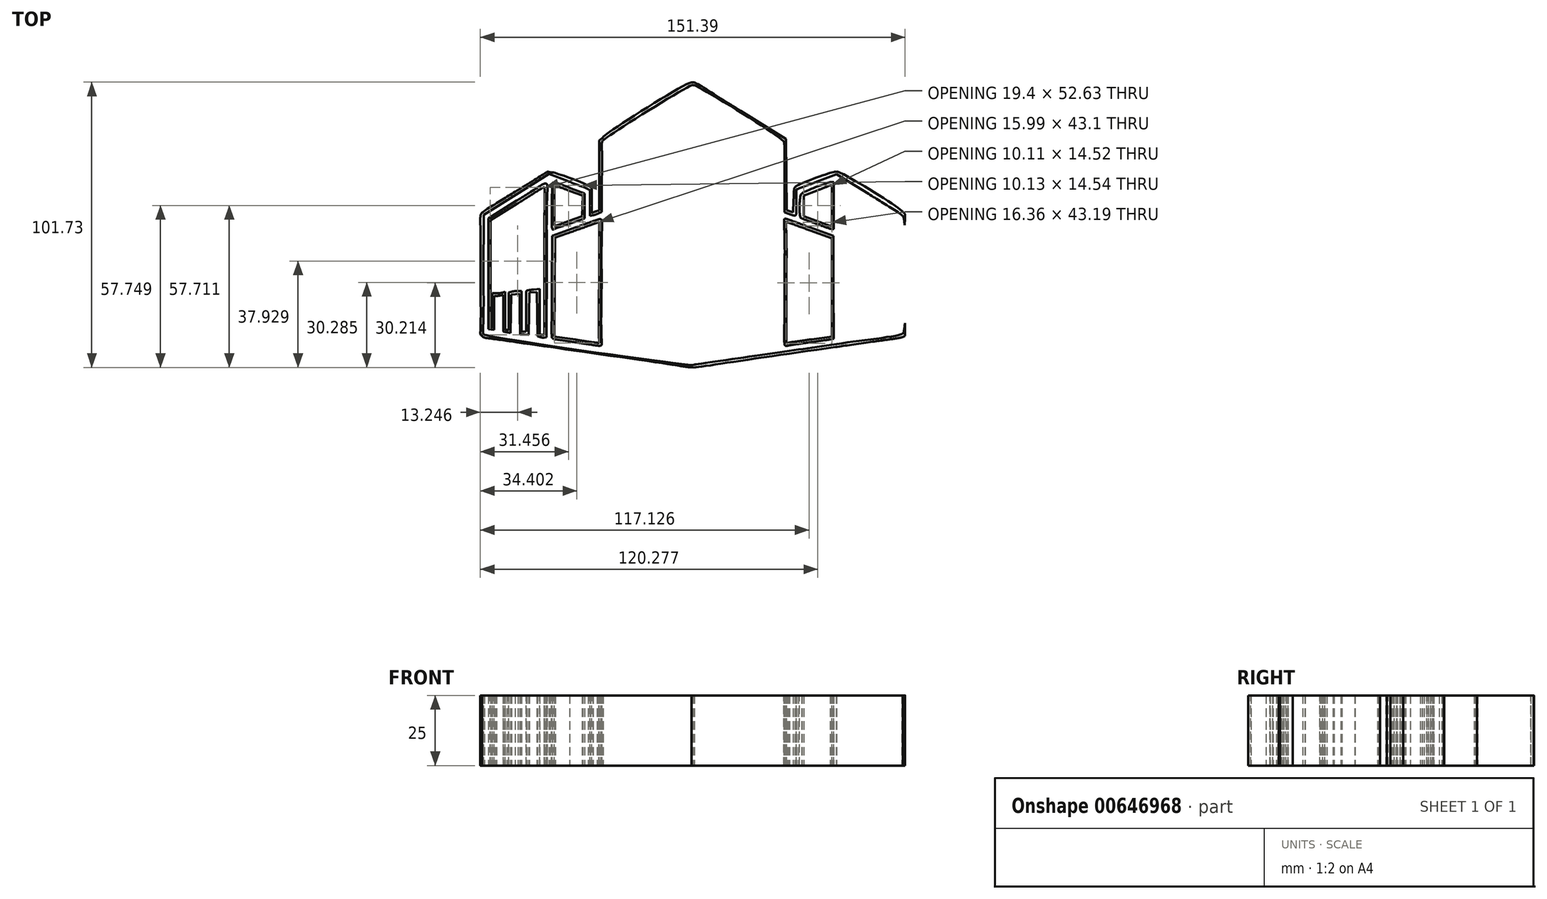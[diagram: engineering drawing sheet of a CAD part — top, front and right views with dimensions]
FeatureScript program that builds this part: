
annotation { "Feature Type Name" : "Feature", "Feature Type Description" : "" }
export const myFeature = defineFeature(function(context is Context, id is Id, definition is map)
    precondition{}
    {
        {
            var Q0;
            Q0=qCreatedBy(makeId("Top.planeOp"),FACE);
            var sketch = newSketch(context, id + "F0", { "sketchPlane" : qUnion([Q0])});
            skFitSpline(sketch, "E0", {"points": [v(-114.85, -77.61) * mm, v(-115.26, -77.27) * mm, v(-115.37, -76.9) * mm, v(-115.21, -76.34) * mm]});
            skFitSpline(sketch, "E1", {"points": [v(34.93, -23.44) * mm, v(31.93, -22.97) * mm, v(1.1, -18.5) * mm, v(-22.97, -15.06) * mm]});
            skFitSpline(sketch, "E2", {"points": [v(-22.97, -15.06) * mm, v(-31.14, -13.89) * mm, v(-35.02, -13.19) * mm, v(-35.42, -12.82) * mm]});
            skFitSpline(sketch, "E3", {"points": [v(-35.42, -12.82) * mm, v(-35.95, -12.32) * mm, v(-35.98, -10.82) * mm, v(-35.98, 9) * mm]});
            skFitSpline(sketch, "E4", {"points": [v(-35.98, 9) * mm, v(-35.98, 25.48) * mm, v(-35.9, 30.43) * mm, v(-35.58, 30.88) * mm]});
            skFitSpline(sketch, "E5", {"points": [v(-35.58, 30.88) * mm, v(-35.35, 31.2) * mm, v(-30, 34.68) * mm, v(-23.7, 38.6) * mm]});
            skFitSpline(sketch, "E6", {"points": [v(-23.7, 38.6) * mm, v(-13.38, 45.02) * mm, v(-12.09, 45.73) * mm, v(-11, 45.58) * mm]});
            skFitSpline(sketch, "E7", {"points": [v(-11, 45.58) * mm, v(-9.58, 45.39) * mm, v(2.65, 40.76) * mm, v(3.27, 40.18) * mm]});
            skFitSpline(sketch, "E8", {"points": [v(3.27, 40.18) * mm, v(3.58, 39.9) * mm, v(3.7, 38.59) * mm, v(3.7, 35.43) * mm]});
            skFitSpline(sketch, "E9", {"points": [v(3.7, 35.43) * mm, v(3.7, 31.6) * mm, v(3.76, 31.1) * mm, v(4.22, 31.3) * mm]});
            skFitSpline(sketch, "E10", {"points": [v(4.22, 31.3) * mm, v(4.5, 31.43) * mm, v(5.1, 31.62) * mm, v(5.52, 31.75) * mm]});
            skFitSpline(sketch, "E11", {"points": [v(7.36, 57.77) * mm, v(9.81, 59.8) * mm, v(38.9, 77.62) * mm, v(39.74, 77.61) * mm]});
            skFitSpline(sketch, "E12", {"points": [v(39.74, 77.61) * mm, v(40.28, 77.6) * mm, v(46.84, 73.7) * mm, v(56.73, 67.51) * mm]});
            skFitSpline(sketch, "E13", {"points": [v(75.6, 35.54) * mm, v(75.68, 37.9) * mm, v(75.9, 39.99) * mm, v(76.08, 40.17) * mm]});
            skFitSpline(sketch, "E14", {"points": [v(76.08, 40.17) * mm, v(76.62, 40.73) * mm, v(89.88, 45.68) * mm, v(90.82, 45.68) * mm]});
            skFitSpline(sketch, "E15", {"points": [v(90.82, 45.68) * mm, v(91.62, 45.68) * mm, v(113.31, 32.55) * mm, v(114.71, 31.23) * mm]});
            skFitSpline(sketch, "E16", {"points": [v(114.71, 31.23) * mm, v(115.24, 30.72) * mm, v(115.28, 29.2) * mm, v(115.28, 8.96) * mm]});
            skLineSegment(sketch, "E17", {"start": v(5.52, 31.75) * mm, "end": v(6.3, 31.96) * mm});
            skLineSegment(sketch, "E18", {"start": v(6.3, 31.96) * mm, "end": v(6.3, 44.43) * mm});
            skLineSegment(sketch, "E19", {"start": v(6.3, 44.43) * mm, "end": v(6.3, 56.9) * mm});
            skLineSegment(sketch, "E20", {"start": v(6.3, 56.9) * mm, "end": v(7.36, 57.77) * mm});
            skFitSpline(sketch, "E21", {"points": [v(114.55, -13.1) * mm, v(114.15, -13.3) * mm, v(110.82, -13.86) * mm, v(107.15, -14.37) * mm]});
            skFitSpline(sketch, "E22", {"points": [v(107.15, -14.37) * mm, v(103.48, -14.89) * mm, v(96.02, -15.95) * mm, v(90.56, -16.74) * mm]});
            skFitSpline(sketch, "E23", {"points": [v(90.56, -16.74) * mm, v(49.54, -22.69) * mm, v(40.18, -24) * mm, v(39.17, -23.97) * mm]});
            skFitSpline(sketch, "E24", {"points": [v(39.17, -23.97) * mm, v(38.54, -23.95) * mm, v(36.63, -23.71) * mm, v(34.93, -23.44) * mm]});
            skLineSegment(sketch, "E25", {"start": v(56.73, 67.51) * mm, "end": v(72.83, 57.42) * mm});
            skLineSegment(sketch, "E26", {"start": v(72.83, 57.42) * mm, "end": v(73, 44.74) * mm});
            skLineSegment(sketch, "E27", {"start": v(73, 44.74) * mm, "end": v(73.15, 32.07) * mm});
            skLineSegment(sketch, "E28", {"start": v(73.15, 32.07) * mm, "end": v(74.3, 31.66) * mm});
            skLineSegment(sketch, "E29", {"start": v(74.3, 31.66) * mm, "end": v(75.43, 31.24) * mm});
            skLineSegment(sketch, "E30", {"start": v(75.43, 31.24) * mm, "end": v(75.6, 35.54) * mm});
            skFitSpline(sketch, "E31", {"points": [v(77.34, -17.66) * mm, v(97.36, -14.77) * mm, v(113.94, -12.22) * mm, v(114.18, -12) * mm]});
            skFitSpline(sketch, "E32", {"points": [v(114.18, -12) * mm, v(114.81, -11.41) * mm, v(114.85, 29.25) * mm, v(114.22, 30.15) * mm]});
            skFitSpline(sketch, "E33", {"points": [v(114.22, 30.15) * mm, v(114, 30.47) * mm, v(108.67, 33.93) * mm, v(102.37, 37.84) * mm]});
            skFitSpline(sketch, "E34", {"points": [v(83.83, 42.23) * mm, v(79.94, 40.73) * mm, v(76.7, 39.5) * mm, v(76.66, 39.5) * mm]});
            skFitSpline(sketch, "E35", {"points": [v(76.66, 39.5) * mm, v(76.61, 39.5) * mm, v(76.57, 37.48) * mm, v(76.57, 35) * mm]});
            skFitSpline(sketch, "E36", {"points": [v(76.57, 35) * mm, v(76.57, 32.4) * mm, v(76.43, 30.38) * mm, v(76.25, 30.25) * mm]});
            skFitSpline(sketch, "E37", {"points": [v(76.25, 30.25) * mm, v(76.07, 30.13) * mm, v(75.12, 30.32) * mm, v(74.13, 30.66) * mm]});
            skLineSegment(sketch, "E38", {"start": v(115.28, 8.96) * mm, "end": v(115.28, -12.77) * mm});
            skLineSegment(sketch, "E39", {"start": v(115.28, -12.77) * mm, "end": v(114.55, -13.1) * mm});
            skFitSpline(sketch, "E40", {"points": [v(72.34, 43.66) * mm, v(72.34, 50.46) * mm, v(72.22, 56.2) * mm, v(72.1, 56.42) * mm]});
            skFitSpline(sketch, "E41", {"points": [v(72.1, 56.42) * mm, v(71.77, 56.96) * mm, v(40.43, 76.56) * mm, v(39.8, 76.62) * mm]});
            skFitSpline(sketch, "E42", {"points": [v(39.8, 76.62) * mm, v(39.36, 76.67) * mm, v(8.83, 57.85) * mm, v(7.69, 56.84) * mm]});
            skFitSpline(sketch, "E43", {"points": [v(7.69, 56.84) * mm, v(7.38, 56.56) * mm, v(7.28, 53.55) * mm, v(7.28, 43.98) * mm]});
            skLineSegment(sketch, "E44", {"start": v(102.37, 37.84) * mm, "end": v(90.92, 44.95) * mm});
            skLineSegment(sketch, "E45", {"start": v(90.92, 44.95) * mm, "end": v(83.83, 42.23) * mm});
            skFitSpline(sketch, "E46", {"points": [v(6.22, 31) * mm, v(5.64, 30.73) * mm, v(4.7, 30.4) * mm, v(4.1, 30.26) * mm]});
            skLineSegment(sketch, "E47", {"start": v(74.13, 30.66) * mm, "end": v(72.34, 31.3) * mm});
            skLineSegment(sketch, "E48", {"start": v(72.34, 31.3) * mm, "end": v(72.34, 43.66) * mm});
            skFitSpline(sketch, "E49", {"points": [v(3.05, 34.57) * mm, v(3.05, 38.73) * mm, v(3, 39.15) * mm, v(2.41, 39.5) * mm]});
            skFitSpline(sketch, "E50", {"points": [v(2.41, 39.5) * mm, v(2.06, 39.71) * mm, v(-1.23, 41.03) * mm, v(-4.89, 42.43) * mm]});
            skLineSegment(sketch, "E51", {"start": v(7.28, 43.98) * mm, "end": v(7.28, 31.49) * mm});
            skLineSegment(sketch, "E52", {"start": v(7.28, 31.49) * mm, "end": v(6.22, 31) * mm});
            skFitSpline(sketch, "E53", {"points": [v(-34.93, 9.18) * mm, v(-35, -8.5) * mm, v(-34.94, -12.08) * mm, v(-34.57, -12.24) * mm]});
            skFitSpline(sketch, "E54", {"points": [v(-34.57, -12.24) * mm, v(-33.8, -12.57) * mm, v(39.61, -23.14) * mm, v(40.3, -23.02) * mm]});
            skFitSpline(sketch, "E55", {"points": [v(40.3, -23.02) * mm, v(40.66, -22.96) * mm, v(57.33, -20.54) * mm, v(77.34, -17.66) * mm]});
            skLineSegment(sketch, "E56", {"start": v(4.1, 30.26) * mm, "end": v(3.05, 30.01) * mm});
            skLineSegment(sketch, "E57", {"start": v(3.05, 30.01) * mm, "end": v(3.05, 34.57) * mm});
            skLineSegment(sketch, "E58", {"start": v(-4.89, 42.43) * mm, "end": v(-11.54, 44.97) * mm});
            skLineSegment(sketch, "E59", {"start": v(-11.54, 44.97) * mm, "end": v(-23.2, 37.7) * mm});
            skLineSegment(sketch, "E60", {"start": v(-23.2, 37.7) * mm, "end": v(-34.85, 30.42) * mm});
            skLineSegment(sketch, "E61", {"start": v(-34.85, 30.42) * mm, "end": v(-34.93, 9.18) * mm});
            skFitSpline(sketch, "E62", {"points": [v(32.4, 7.65) * mm, v(31.56, 7.59) * mm, v(30.54, 7.46) * mm, v(30.13, 7.36) * mm]});
            skLineSegment(sketch, "E63", {"start": v(77.34, -17.66) * mm, "end": v(77.34, -17.66) * mm});
            skFitSpline(sketch, "E64", {"points": [v(24.56, 6.84) * mm, v(23.87, 6.84) * mm, v(22.85, 6.74) * mm, v(22.29, 6.62) * mm]});
            skLineSegment(sketch, "E65", {"start": v(35.1, -20.43) * mm, "end": v(34.12, -20.2) * mm});
            skLineSegment(sketch, "E66", {"start": v(34.12, -20.2) * mm, "end": v(34.03, -6.22) * mm});
            skLineSegment(sketch, "E67", {"start": v(34.03, -6.22) * mm, "end": v(33.95, 7.75) * mm});
            skLineSegment(sketch, "E68", {"start": v(33.95, 7.75) * mm, "end": v(32.4, 7.65) * mm});
            skFitSpline(sketch, "E69", {"points": [v(19.9, -18.13) * mm, v(19.24, -18.2) * mm, v(18.4, -18.07) * mm, v(18.03, -17.85) * mm]});
            skFitSpline(sketch, "E70", {"points": [v(18.03, -17.85) * mm, v(17.38, -17.46) * mm, v(17.37, -17.16) * mm, v(17.37, -5.62) * mm]});
            skLineSegment(sketch, "E71", {"start": v(30.13, 7.36) * mm, "end": v(29.4, 7.2) * mm});
            skLineSegment(sketch, "E72", {"start": v(29.4, 7.2) * mm, "end": v(29.4, -6.07) * mm});
            skLineSegment(sketch, "E73", {"start": v(29.4, -6.07) * mm, "end": v(29.4, -19.33) * mm});
            skLineSegment(sketch, "E74", {"start": v(29.4, -19.33) * mm, "end": v(27.7, -19.22) * mm});
            skLineSegment(sketch, "E75", {"start": v(27.7, -19.22) * mm, "end": v(25.99, -19.11) * mm});
            skLineSegment(sketch, "E76", {"start": v(25.99, -19.11) * mm, "end": v(25.9, -6.13) * mm});
            skLineSegment(sketch, "E77", {"start": v(25.9, -6.13) * mm, "end": v(25.81, 6.84) * mm});
            skLineSegment(sketch, "E78", {"start": v(25.81, 6.84) * mm, "end": v(24.56, 6.84) * mm});
            skFitSpline(sketch, "E79", {"points": [v(15.66, 5.99) * mm, v(14.72, 5.86) * mm, v(13.7, 5.76) * mm, v(13.38, 5.76) * mm]});
            skFitSpline(sketch, "E80", {"points": [v(13.38, 5.76) * mm, v(12.85, 5.75) * mm, v(12.81, 4.96) * mm, v(12.81, -5.73) * mm]});
            skLineSegment(sketch, "E81", {"start": v(22.29, 6.62) * mm, "end": v(21.28, 6.39) * mm});
            skLineSegment(sketch, "E82", {"start": v(21.28, 6.39) * mm, "end": v(21.2, -5.82) * mm});
            skLineSegment(sketch, "E83", {"start": v(21.2, -5.82) * mm, "end": v(21.1, -18.02) * mm});
            skLineSegment(sketch, "E84", {"start": v(21.1, -18.02) * mm, "end": v(19.9, -18.13) * mm});
            skFitSpline(sketch, "E85", {"points": [v(11.1, -16.96) * mm, v(10.16, -16.82) * mm, v(9.28, -16.58) * mm, v(9.15, -16.44) * mm]});
            skFitSpline(sketch, "E86", {"points": [v(9.15, -16.44) * mm, v(9.01, -16.29) * mm, v(8.94, -0.04) * mm, v(8.99, 19.67) * mm]});
            skLineSegment(sketch, "E87", {"start": v(17.37, -5.62) * mm, "end": v(17.37, 6.22) * mm});
            skLineSegment(sketch, "E88", {"start": v(17.37, 6.22) * mm, "end": v(15.66, 5.99) * mm});
            skFitSpline(sketch, "E89", {"points": [v(10.49, 56.4) * mm, v(11.26, 56.89) * mm, v(12.03, 57.3) * mm, v(12.2, 57.3) * mm]});
            skFitSpline(sketch, "E90", {"points": [v(12.2, 57.3) * mm, v(12.36, 57.3) * mm, v(12.49, 52) * mm, v(12.49, 44.93) * mm]});
            skLineSegment(sketch, "E91", {"start": v(12.81, -5.73) * mm, "end": v(12.81, -17.2) * mm});
            skLineSegment(sketch, "E92", {"start": v(12.81, -17.2) * mm, "end": v(11.1, -16.96) * mm});
            skFitSpline(sketch, "E93", {"points": [v(13.22, 32.82) * mm, v(13.62, 32.96) * mm, v(14.68, 33.36) * mm, v(15.58, 33.7) * mm]});
            skLineSegment(sketch, "E94", {"start": v(8.99, 19.67) * mm, "end": v(9.07, 55.5) * mm});
            skLineSegment(sketch, "E95", {"start": v(9.07, 55.5) * mm, "end": v(10.49, 56.4) * mm});
            skFitSpline(sketch, "E96", {"points": [v(18.75, 61.56) * mm, v(19.5, 62) * mm, v(20.31, 62.38) * mm, v(20.54, 62.38) * mm]});
            skFitSpline(sketch, "E97", {"points": [v(20.54, 62.38) * mm, v(20.85, 62.37) * mm, v(20.94, 59.45) * mm, v(20.94, 49) * mm]});
            skLineSegment(sketch, "E98", {"start": v(12.49, 44.93) * mm, "end": v(12.49, 32.56) * mm});
            skLineSegment(sketch, "E99", {"start": v(12.49, 32.56) * mm, "end": v(13.22, 32.82) * mm});
            skFitSpline(sketch, "E100", {"points": [v(26.8, 66.54) * mm, v(29.22, 68.26) * mm, v(29.08, 69.14) * mm, v(29.08, 52.99) * mm]});
            skLineSegment(sketch, "E101", {"start": v(15.58, 33.7) * mm, "end": v(17.2, 34.31) * mm});
            skLineSegment(sketch, "E102", {"start": v(17.2, 34.31) * mm, "end": v(17.29, 47.53) * mm});
            skLineSegment(sketch, "E103", {"start": v(17.29, 47.53) * mm, "end": v(17.37, 60.75) * mm});
            skLineSegment(sketch, "E104", {"start": v(17.37, 60.75) * mm, "end": v(18.75, 61.56) * mm});
            skFitSpline(sketch, "E105", {"points": [v(35.9, 72.26) * mm, v(37.07, 73) * mm, v(38.2, 73.63) * mm, v(38.43, 73.63) * mm]});
            skFitSpline(sketch, "E106", {"points": [v(38.43, 73.63) * mm, v(38.75, 73.63) * mm, v(38.84, 64.04) * mm, v(38.84, 26.44) * mm]});
            skLineSegment(sketch, "E107", {"start": v(20.94, 49) * mm, "end": v(20.94, 35.6) * mm});
            skLineSegment(sketch, "E108", {"start": v(20.94, 35.6) * mm, "end": v(23.22, 36.38) * mm});
            skLineSegment(sketch, "E109", {"start": v(23.22, 36.38) * mm, "end": v(25.5, 37.15) * mm});
            skLineSegment(sketch, "E110", {"start": v(25.5, 37.15) * mm, "end": v(25.5, 51.4) * mm});
            skLineSegment(sketch, "E111", {"start": v(25.5, 51.4) * mm, "end": v(25.5, 65.63) * mm});
            skLineSegment(sketch, "E112", {"start": v(25.5, 65.63) * mm, "end": v(26.8, 66.54) * mm});
            skFitSpline(sketch, "E113", {"points": [v(37.45, -20.7) * mm, v(36.7, -20.68) * mm, v(35.63, -20.55) * mm, v(35.1, -20.42) * mm]});
            skLineSegment(sketch, "E114", {"start": v(29.08, 52.99) * mm, "end": v(29.08, 38.52) * mm});
            skLineSegment(sketch, "E115", {"start": v(29.08, 38.52) * mm, "end": v(31.35, 39.27) * mm});
            skLineSegment(sketch, "E116", {"start": v(31.35, 39.27) * mm, "end": v(33.62, 40.01) * mm});
            skLineSegment(sketch, "E117", {"start": v(33.62, 40.01) * mm, "end": v(33.7, 55.45) * mm});
            skLineSegment(sketch, "E118", {"start": v(33.7, 55.45) * mm, "end": v(33.8, 70.88) * mm});
            skLineSegment(sketch, "E119", {"start": v(33.8, 70.88) * mm, "end": v(35.9, 72.26) * mm});
            skFitSpline(sketch, "E120", {"points": [v(31.84, 38.36) * mm, v(30.4, 37.83) * mm, v(29.06, 37.38) * mm, v(28.83, 37.36) * mm]});
            skFitSpline(sketch, "E121", {"points": [v(28.83, 37.36) * mm, v(28.51, 37.34) * mm, v(28.43, 40.46) * mm, v(28.43, 51.86) * mm]});
            skLineSegment(sketch, "E122", {"start": v(38.84, 26.44) * mm, "end": v(38.84, -20.74) * mm});
            skLineSegment(sketch, "E123", {"start": v(38.84, -20.74) * mm, "end": v(37.45, -20.7) * mm});
            skFitSpline(sketch, "E124", {"points": [v(23.55, 35.43) * mm, v(22.03, 34.88) * mm, v(20.6, 34.5) * mm, v(20.37, 34.6) * mm]});
            skFitSpline(sketch, "E125", {"points": [v(20.37, 34.6) * mm, v(20.06, 34.73) * mm, v(19.97, 37.71) * mm, v(19.97, 47.84) * mm]});
            skFitSpline(sketch, "E126", {"points": [v(19.97, 47.84) * mm, v(19.97, 55.04) * mm, v(19.85, 60.92) * mm, v(19.71, 60.92) * mm]});
            skFitSpline(sketch, "E127", {"points": [v(19.71, 60.92) * mm, v(19.58, 60.92) * mm, v(19.14, 60.67) * mm, v(18.74, 60.36) * mm]});
            skLineSegment(sketch, "E128", {"start": v(37.86, 26.27) * mm, "end": v(37.86, 72.19) * mm});
            skLineSegment(sketch, "E129", {"start": v(37.86, 72.19) * mm, "end": v(36.24, 71.27) * mm});
            skLineSegment(sketch, "E130", {"start": v(36.24, 71.27) * mm, "end": v(34.61, 70.35) * mm});
            skLineSegment(sketch, "E131", {"start": v(34.61, 70.35) * mm, "end": v(34.53, 54.84) * mm});
            skLineSegment(sketch, "E132", {"start": v(34.53, 54.84) * mm, "end": v(34.44, 39.33) * mm});
            skLineSegment(sketch, "E133", {"start": v(34.44, 39.33) * mm, "end": v(31.84, 38.36) * mm});
            skFitSpline(sketch, "E134", {"points": [v(15.31, 32.5) * mm, v(13.83, 31.96) * mm, v(12.44, 31.52) * mm, v(12.22, 31.52) * mm]});
            skFitSpline(sketch, "E135", {"points": [v(12.22, 31.52) * mm, v(11.93, 31.52) * mm, v(11.84, 34.52) * mm, v(11.84, 43.68) * mm]});
            skFitSpline(sketch, "E136", {"points": [v(11.84, 43.68) * mm, v(11.84, 50.54) * mm, v(11.7, 55.84) * mm, v(11.55, 55.84) * mm]});
            skFitSpline(sketch, "E137", {"points": [v(11.55, 55.84) * mm, v(11.39, 55.84) * mm, v(10.94, 55.56) * mm, v(10.56, 55.2) * mm]});
            skLineSegment(sketch, "E138", {"start": v(28.43, 51.86) * mm, "end": v(28.43, 66.39) * mm});
            skLineSegment(sketch, "E139", {"start": v(28.43, 66.39) * mm, "end": v(27.45, 65.82) * mm});
            skLineSegment(sketch, "E140", {"start": v(27.45, 65.82) * mm, "end": v(26.48, 65.26) * mm});
            skLineSegment(sketch, "E141", {"start": v(26.48, 65.26) * mm, "end": v(26.4, 50.85) * mm});
            skLineSegment(sketch, "E142", {"start": v(26.4, 50.85) * mm, "end": v(26.31, 36.43) * mm});
            skLineSegment(sketch, "E143", {"start": v(26.31, 36.43) * mm, "end": v(23.55, 35.43) * mm});
            skFitSpline(sketch, "E144", {"points": [v(12.9, 6.63) * mm, v(13.3, 6.72) * mm, v(14.69, 6.9) * mm, v(15.98, 7.02) * mm]});
            skLineSegment(sketch, "E145", {"start": v(18.74, 60.36) * mm, "end": v(18.02, 59.8) * mm});
            skLineSegment(sketch, "E146", {"start": v(18.02, 59.8) * mm, "end": v(18.02, 46.64) * mm});
            skLineSegment(sketch, "E147", {"start": v(18.02, 46.64) * mm, "end": v(18.02, 33.49) * mm});
            skLineSegment(sketch, "E148", {"start": v(18.02, 33.49) * mm, "end": v(15.31, 32.5) * mm});
            skFitSpline(sketch, "E149", {"points": [v(20.3, -4.98) * mm, v(20.3, 1.7) * mm, v(20.4, 7.23) * mm, v(20.54, 7.32) * mm]});
            skFitSpline(sketch, "E150", {"points": [v(20.54, 7.32) * mm, v(20.67, 7.4) * mm, v(22.06, 7.6) * mm, v(23.63, 7.74) * mm]});
            skLineSegment(sketch, "E151", {"start": v(10.56, 55.2) * mm, "end": v(9.87, 54.57) * mm});
            skLineSegment(sketch, "E152", {"start": v(9.87, 54.57) * mm, "end": v(9.96, 19.36) * mm});
            skLineSegment(sketch, "E153", {"start": v(9.96, 19.36) * mm, "end": v(10.05, -15.84) * mm});
            skLineSegment(sketch, "E154", {"start": v(10.05, -15.84) * mm, "end": v(11.1, -15.96) * mm});
            skLineSegment(sketch, "E155", {"start": v(11.1, -15.96) * mm, "end": v(12.16, -16.07) * mm});
            skLineSegment(sketch, "E156", {"start": v(12.16, -16.07) * mm, "end": v(12.16, -4.8) * mm});
            skLineSegment(sketch, "E157", {"start": v(12.16, -4.8) * mm, "end": v(12.16, 6.46) * mm});
            skLineSegment(sketch, "E158", {"start": v(12.16, 6.46) * mm, "end": v(12.9, 6.63) * mm});
            skFitSpline(sketch, "E159", {"points": [v(26.47, -5.1) * mm, v(26.47, -16.17) * mm, v(26.55, -18.2) * mm, v(26.94, -18.2) * mm]});
            skFitSpline(sketch, "E160", {"points": [v(26.94, -18.2) * mm, v(27.19, -18.2) * mm, v(27.63, -18.3) * mm, v(27.9, -18.42) * mm]});
            skFitSpline(sketch, "E161", {"points": [v(27.9, -18.42) * mm, v(28.36, -18.62) * mm, v(28.43, -17.24) * mm, v(28.5, -5.26) * mm]});
            skLineSegment(sketch, "E162", {"start": v(15.98, 7.02) * mm, "end": v(18.34, 7.25) * mm});
            skLineSegment(sketch, "E163", {"start": v(18.34, 7.25) * mm, "end": v(18.34, -4.93) * mm});
            skLineSegment(sketch, "E164", {"start": v(18.34, -4.93) * mm, "end": v(18.34, -17.11) * mm});
            skLineSegment(sketch, "E165", {"start": v(18.34, -17.11) * mm, "end": v(19.32, -17.11) * mm});
            skLineSegment(sketch, "E166", {"start": v(19.32, -17.11) * mm, "end": v(20.3, -17.11) * mm});
            skLineSegment(sketch, "E167", {"start": v(20.3, -17.11) * mm, "end": v(20.3, -4.98) * mm});
            skFitSpline(sketch, "E168", {"points": [v(31.25, 8.43) * mm, v(32.72, 8.6) * mm, v(34.14, 8.65) * mm, v(34.42, 8.53) * mm]});
            skFitSpline(sketch, "E169", {"points": [v(34.42, 8.53) * mm, v(34.87, 8.34) * mm, v(34.93, 6.7) * mm, v(34.93, -5.43) * mm]});
            skFitSpline(sketch, "E170", {"points": [v(34.93, -5.43) * mm, v(34.93, -12.99) * mm, v(35.03, -19.28) * mm, v(35.15, -19.41) * mm]});
            skFitSpline(sketch, "E171", {"points": [v(35.15, -19.41) * mm, v(35.27, -19.55) * mm, v(35.93, -19.65) * mm, v(36.61, -19.65) * mm]});
            skLineSegment(sketch, "E172", {"start": v(23.63, 7.74) * mm, "end": v(26.47, 8) * mm});
            skLineSegment(sketch, "E173", {"start": v(26.47, 8) * mm, "end": v(26.47, -5.1) * mm});
            skFitSpline(sketch, "E174", {"points": [v(40.79, 26.4) * mm, v(40.79, 52.86) * mm, v(40.91, 73.63) * mm, v(41.07, 73.63) * mm]});
            skFitSpline(sketch, "E175", {"points": [v(41.07, 73.63) * mm, v(41.22, 73.63) * mm, v(42.32, 73.03) * mm, v(43.5, 72.3) * mm]});
            skLineSegment(sketch, "E176", {"start": v(28.5, -5.26) * mm, "end": v(28.59, 8.11) * mm});
            skLineSegment(sketch, "E177", {"start": v(28.59, 8.11) * mm, "end": v(31.25, 8.43) * mm});
            skFitSpline(sketch, "E178", {"points": [v(50.22, 52.96) * mm, v(50.22, 69.14) * mm, v(50.06, 68.2) * mm, v(52.5, 66.64) * mm]});
            skLineSegment(sketch, "E179", {"start": v(36.61, -19.65) * mm, "end": v(37.86, -19.65) * mm});
            skLineSegment(sketch, "E180", {"start": v(37.86, -19.65) * mm, "end": v(37.86, 26.27) * mm});
            skFitSpline(sketch, "E181", {"points": [v(55.59, 36.6) * mm, v(56.48, 36.26) * mm, v(57.54, 35.87) * mm, v(57.95, 35.73) * mm]});
            skLineSegment(sketch, "E182", {"start": v(43.5, 72.3) * mm, "end": v(45.66, 70.95) * mm});
            skLineSegment(sketch, "E183", {"start": v(45.66, 70.95) * mm, "end": v(45.74, 55.54) * mm});
            skLineSegment(sketch, "E184", {"start": v(45.74, 55.54) * mm, "end": v(45.83, 40.12) * mm});
            skLineSegment(sketch, "E185", {"start": v(45.83, 40.12) * mm, "end": v(48.03, 39.3) * mm});
            skLineSegment(sketch, "E186", {"start": v(48.03, 39.3) * mm, "end": v(50.22, 38.47) * mm});
            skLineSegment(sketch, "E187", {"start": v(50.22, 38.47) * mm, "end": v(50.22, 52.96) * mm});
            skFitSpline(sketch, "E188", {"points": [v(58.68, 48.92) * mm, v(58.68, 58.25) * mm, v(58.79, 62.37) * mm, v(59.03, 62.37) * mm]});
            skFitSpline(sketch, "E189", {"points": [v(59.03, 62.37) * mm, v(59.22, 62.37) * mm, v(60.02, 61.95) * mm, v(60.82, 61.43) * mm]});
            skLineSegment(sketch, "E190", {"start": v(52.5, 66.64) * mm, "end": v(53.79, 65.82) * mm});
            skLineSegment(sketch, "E191", {"start": v(53.79, 65.82) * mm, "end": v(53.88, 51.52) * mm});
            skLineSegment(sketch, "E192", {"start": v(53.88, 51.52) * mm, "end": v(53.96, 37.22) * mm});
            skLineSegment(sketch, "E193", {"start": v(53.96, 37.22) * mm, "end": v(55.59, 36.6) * mm});
            skFitSpline(sketch, "E194", {"points": [v(64.13, 33.54) * mm, v(65.16, 33.18) * mm, v(66.18, 32.8) * mm, v(66.4, 32.7) * mm]});
            skFitSpline(sketch, "E195", {"points": [v(66.4, 32.7) * mm, v(66.73, 32.57) * mm, v(66.81, 35.16) * mm, v(66.81, 44.91) * mm]});
            skFitSpline(sketch, "E196", {"points": [v(66.81, 44.91) * mm, v(66.81, 53.48) * mm, v(66.92, 57.3) * mm, v(67.16, 57.3) * mm]});
            skFitSpline(sketch, "E197", {"points": [v(67.16, 57.3) * mm, v(67.35, 57.3) * mm, v(68.16, 56.87) * mm, v(68.95, 56.35) * mm]});
            skLineSegment(sketch, "E198", {"start": v(57.95, 35.73) * mm, "end": v(58.68, 35.47) * mm});
            skLineSegment(sketch, "E199", {"start": v(58.68, 35.47) * mm, "end": v(58.68, 48.92) * mm});
            skFitSpline(sketch, "E200", {"points": [v(70.39, 19.53) * mm, v(70.39, -0.2) * mm, v(70.28, -16.42) * mm, v(70.15, -16.51) * mm]});
            skFitSpline(sketch, "E201", {"points": [v(70.15, -16.51) * mm, v(70.01, -16.6) * mm, v(69.2, -16.8) * mm, v(68.36, -16.94) * mm]});
            skLineSegment(sketch, "E202", {"start": v(60.82, 61.43) * mm, "end": v(62.26, 60.5) * mm});
            skLineSegment(sketch, "E203", {"start": v(62.26, 60.5) * mm, "end": v(62.26, 47.34) * mm});
            skLineSegment(sketch, "E204", {"start": v(62.26, 47.34) * mm, "end": v(62.26, 34.2) * mm});
            skLineSegment(sketch, "E205", {"start": v(62.26, 34.2) * mm, "end": v(64.13, 33.54) * mm});
            skFitSpline(sketch, "E206", {"points": [v(65.1, 5.88) * mm, v(64.16, 6) * mm, v(63.14, 6.11) * mm, v(62.83, 6.11) * mm]});
            skFitSpline(sketch, "E207", {"points": [v(62.83, 6.11) * mm, v(62.3, 6.11) * mm, v(62.26, 5.3) * mm, v(62.26, -5.82) * mm]});
            skLineSegment(sketch, "E208", {"start": v(68.95, 56.35) * mm, "end": v(70.39, 55.4) * mm});
            skLineSegment(sketch, "E209", {"start": v(70.39, 55.4) * mm, "end": v(70.39, 19.53) * mm});
            skFitSpline(sketch, "E210", {"points": [v(61.24, -17.98) * mm, v(60.68, -18.1) * mm, v(59.88, -18.2) * mm, v(59.45, -18.2) * mm]});
            skLineSegment(sketch, "E211", {"start": v(68.36, -16.94) * mm, "end": v(66.81, -17.2) * mm});
            skLineSegment(sketch, "E212", {"start": v(66.81, -17.2) * mm, "end": v(66.81, -5.77) * mm});
            skLineSegment(sketch, "E213", {"start": v(66.81, -5.77) * mm, "end": v(66.81, 5.65) * mm});
            skLineSegment(sketch, "E214", {"start": v(66.81, 5.65) * mm, "end": v(65.1, 5.88) * mm});
            skFitSpline(sketch, "E215", {"points": [v(57.46, 6.6) * mm, v(56.79, 6.73) * mm, v(55.7, 6.84) * mm, v(55.02, 6.84) * mm]});
            skLineSegment(sketch, "E216", {"start": v(62.26, -5.82) * mm, "end": v(62.26, -17.75) * mm});
            skLineSegment(sketch, "E217", {"start": v(62.26, -17.75) * mm, "end": v(61.24, -17.98) * mm});
            skFitSpline(sketch, "E218", {"points": [v(49.49, 7.36) * mm, v(49.09, 7.46) * mm, v(48.06, 7.59) * mm, v(47.21, 7.65) * mm]});
            skLineSegment(sketch, "E219", {"start": v(59.45, -18.2) * mm, "end": v(58.68, -18.2) * mm});
            skLineSegment(sketch, "E220", {"start": v(58.68, -18.2) * mm, "end": v(58.68, -5.9) * mm});
            skLineSegment(sketch, "E221", {"start": v(58.68, -5.9) * mm, "end": v(58.68, 6.38) * mm});
            skLineSegment(sketch, "E222", {"start": v(58.68, 6.38) * mm, "end": v(57.46, 6.6) * mm});
            skFitSpline(sketch, "E223", {"points": [v(45.67, -6.11) * mm, v(45.67, -13.74) * mm, v(45.54, -20.06) * mm, v(45.4, -20.16) * mm]});
            skFitSpline(sketch, "E224", {"points": [v(45.4, -20.16) * mm, v(45.25, -20.26) * mm, v(44.15, -20.46) * mm, v(42.96, -20.6) * mm]});
            skLineSegment(sketch, "E225", {"start": v(55.02, 6.84) * mm, "end": v(53.8, 6.84) * mm});
            skLineSegment(sketch, "E226", {"start": v(53.8, 6.84) * mm, "end": v(53.72, -6.13) * mm});
            skLineSegment(sketch, "E227", {"start": v(53.72, -6.13) * mm, "end": v(53.64, -19.11) * mm});
            skLineSegment(sketch, "E228", {"start": v(53.64, -19.11) * mm, "end": v(51.93, -19.22) * mm});
            skLineSegment(sketch, "E229", {"start": v(51.93, -19.22) * mm, "end": v(50.22, -19.33) * mm});
            skLineSegment(sketch, "E230", {"start": v(50.22, -19.33) * mm, "end": v(50.22, -6.07) * mm});
            skLineSegment(sketch, "E231", {"start": v(50.22, -6.07) * mm, "end": v(50.22, 7.2) * mm});
            skLineSegment(sketch, "E232", {"start": v(50.22, 7.2) * mm, "end": v(49.49, 7.36) * mm});
            skLineSegment(sketch, "E233", {"start": v(47.21, 7.65) * mm, "end": v(45.67, 7.75) * mm});
            skLineSegment(sketch, "E234", {"start": v(45.67, 7.75) * mm, "end": v(45.67, -6.11) * mm});
            skFitSpline(sketch, "E235", {"points": [v(44.7, -5.48) * mm, v(44.7, 6.7) * mm, v(44.75, 8.34) * mm, v(45.2, 8.53) * mm]});
            skFitSpline(sketch, "E236", {"points": [v(45.2, 8.53) * mm, v(45.48, 8.65) * mm, v(46.9, 8.6) * mm, v(48.37, 8.43) * mm]});
            skLineSegment(sketch, "E237", {"start": v(42.96, -20.6) * mm, "end": v(40.79, -20.84) * mm});
            skLineSegment(sketch, "E238", {"start": v(40.79, -20.84) * mm, "end": v(40.79, 26.4) * mm});
            skFitSpline(sketch, "E239", {"points": [v(55.15, 7.8) * mm, v(56.25, 7.67) * mm, v(57.64, 7.57) * mm, v(58.24, 7.57) * mm]});
            skLineSegment(sketch, "E240", {"start": v(43.96, -19.44) * mm, "end": v(44.7, -19.28) * mm});
            skLineSegment(sketch, "E241", {"start": v(44.7, -19.28) * mm, "end": v(44.7, -5.48) * mm});
            skFitSpline(sketch, "E242", {"points": [v(63.88, 6.9) * mm, v(67.87, 6.72) * mm, v(67.46, 8.06) * mm, v(67.46, -4.82) * mm]});
            skLineSegment(sketch, "E243", {"start": v(48.37, 8.43) * mm, "end": v(51.03, 8.11) * mm});
            skLineSegment(sketch, "E244", {"start": v(51.03, 8.11) * mm, "end": v(51.12, -5.16) * mm});
            skLineSegment(sketch, "E245", {"start": v(51.12, -5.16) * mm, "end": v(51.2, -18.44) * mm});
            skLineSegment(sketch, "E246", {"start": v(51.2, -18.44) * mm, "end": v(52.18, -18.28) * mm});
            skLineSegment(sketch, "E247", {"start": v(52.18, -18.28) * mm, "end": v(53.15, -18.12) * mm});
            skLineSegment(sketch, "E248", {"start": v(53.15, -18.12) * mm, "end": v(53.15, -5.04) * mm});
            skLineSegment(sketch, "E249", {"start": v(53.15, -5.04) * mm, "end": v(53.15, 8.03) * mm});
            skLineSegment(sketch, "E250", {"start": v(53.15, 8.03) * mm, "end": v(55.15, 7.8) * mm});
            skFitSpline(sketch, "E251", {"points": [v(68.59, 55.42) * mm, v(68.13, 55.65) * mm, v(67.7, 55.84) * mm, v(67.6, 55.84) * mm]});
            skFitSpline(sketch, "E252", {"points": [v(67.6, 55.84) * mm, v(67.53, 55.84) * mm, v(67.46, 50.36) * mm, v(67.46, 43.65) * mm]});
            skLineSegment(sketch, "E253", {"start": v(58.24, 7.57) * mm, "end": v(59.33, 7.57) * mm});
            skLineSegment(sketch, "E254", {"start": v(59.33, 7.57) * mm, "end": v(59.33, -4.77) * mm});
            skLineSegment(sketch, "E255", {"start": v(59.33, -4.77) * mm, "end": v(59.33, -17.11) * mm});
            skLineSegment(sketch, "E256", {"start": v(59.33, -17.11) * mm, "end": v(60.3, -17.11) * mm});
            skLineSegment(sketch, "E257", {"start": v(60.3, -17.11) * mm, "end": v(61.27, -17.11) * mm});
            skLineSegment(sketch, "E258", {"start": v(61.27, -17.11) * mm, "end": v(61.36, -5.05) * mm});
            skLineSegment(sketch, "E259", {"start": v(61.36, -5.05) * mm, "end": v(61.44, 7.02) * mm});
            skLineSegment(sketch, "E260", {"start": v(61.44, 7.02) * mm, "end": v(63.88, 6.9) * mm});
            skFitSpline(sketch, "E261", {"points": [v(66.4, 31.72) * mm, v(65.82, 31.86) * mm, v(64.47, 32.33) * mm, v(63.4, 32.75) * mm]});
            skLineSegment(sketch, "E262", {"start": v(67.46, -4.82) * mm, "end": v(67.46, -16.07) * mm});
            skLineSegment(sketch, "E263", {"start": v(67.46, -16.07) * mm, "end": v(68.36, -15.96) * mm});
            skLineSegment(sketch, "E264", {"start": v(68.36, -15.96) * mm, "end": v(69.25, -15.84) * mm});
            skLineSegment(sketch, "E265", {"start": v(69.25, -15.84) * mm, "end": v(69.33, 19.58) * mm});
            skLineSegment(sketch, "E266", {"start": v(69.33, 19.58) * mm, "end": v(69.42, 55) * mm});
            skLineSegment(sketch, "E267", {"start": v(69.42, 55) * mm, "end": v(68.59, 55.42) * mm});
            skFitSpline(sketch, "E268", {"points": [v(60.45, 60.5) * mm, v(60, 60.73) * mm, v(59.56, 60.92) * mm, v(59.48, 60.92) * mm]});
            skFitSpline(sketch, "E269", {"points": [v(59.48, 60.92) * mm, v(59.4, 60.92) * mm, v(59.33, 54.96) * mm, v(59.33, 47.67) * mm]});
            skFitSpline(sketch, "E270", {"points": [v(59.33, 47.67) * mm, v(59.33, 40.39) * mm, v(59.22, 34.42) * mm, v(59.09, 34.42) * mm]});
            skFitSpline(sketch, "E271", {"points": [v(59.09, 34.42) * mm, v(58.95, 34.42) * mm, v(57.56, 34.85) * mm, v(56, 35.39) * mm]});
            skLineSegment(sketch, "E272", {"start": v(67.46, 43.65) * mm, "end": v(67.46, 31.47) * mm});
            skLineSegment(sketch, "E273", {"start": v(67.46, 31.47) * mm, "end": v(66.4, 31.72) * mm});
            skFitSpline(sketch, "E274", {"points": [v(52.32, 65.58) * mm, v(51.86, 65.81) * mm, v(51.43, 66) * mm, v(51.34, 66) * mm]});
            skFitSpline(sketch, "E275", {"points": [v(51.34, 66) * mm, v(51.26, 66) * mm, v(51.2, 59.64) * mm, v(51.2, 51.87) * mm]});
            skFitSpline(sketch, "E276", {"points": [v(51.2, 51.87) * mm, v(51.2, 43.57) * mm, v(51.07, 37.65) * mm, v(50.9, 37.53) * mm]});
            skFitSpline(sketch, "E277", {"points": [v(50.9, 37.53) * mm, v(50.73, 37.41) * mm, v(49.3, 37.78) * mm, v(47.72, 38.34) * mm]});
            skLineSegment(sketch, "E278", {"start": v(63.4, 32.75) * mm, "end": v(61.44, 33.52) * mm});
            skLineSegment(sketch, "E279", {"start": v(61.44, 33.52) * mm, "end": v(61.36, 46.8) * mm});
            skLineSegment(sketch, "E280", {"start": v(61.36, 46.8) * mm, "end": v(61.27, 60.08) * mm});
            skLineSegment(sketch, "E281", {"start": v(61.27, 60.08) * mm, "end": v(60.45, 60.5) * mm});
            skFitSpline(sketch, "E282", {"points": [v(43.11, 71.28) * mm, v(42.33, 71.77) * mm, v(41.64, 72.17) * mm, v(41.57, 72.17) * mm]});
            skFitSpline(sketch, "E283", {"points": [v(41.57, 72.17) * mm, v(41.5, 72.17) * mm, v(41.44, 51.45) * mm, v(41.44, 26.13) * mm]});
            skLineSegment(sketch, "E284", {"start": v(56, 35.39) * mm, "end": v(53.15, 36.36) * mm});
            skLineSegment(sketch, "E285", {"start": v(53.15, 36.36) * mm, "end": v(53.15, 50.76) * mm});
            skLineSegment(sketch, "E286", {"start": v(53.15, 50.76) * mm, "end": v(53.15, 65.16) * mm});
            skLineSegment(sketch, "E287", {"start": v(53.15, 65.16) * mm, "end": v(52.32, 65.58) * mm});
            skFitSpline(sketch, "E288", {"points": [v(42.33, -19.76) * mm, v(42.82, -19.68) * mm, v(43.56, -19.54) * mm, v(43.96, -19.44) * mm]});
            skLineSegment(sketch, "E289", {"start": v(47.72, 38.34) * mm, "end": v(44.85, 39.36) * mm});
            skLineSegment(sketch, "E290", {"start": v(44.85, 39.36) * mm, "end": v(44.7, 54.87) * mm});
            skLineSegment(sketch, "E291", {"start": v(44.7, 54.87) * mm, "end": v(44.53, 70.38) * mm});
            skLineSegment(sketch, "E292", {"start": v(44.53, 70.38) * mm, "end": v(43.11, 71.28) * mm});
            skFitSpline(sketch, "E293", {"points": [v(-1.96, -15.1) * mm, v(-6.41, -14.43) * mm, v(-10.18, -13.74) * mm, v(-10.34, -13.57) * mm]});
            skFitSpline(sketch, "E294", {"points": [v(-10.34, -13.57) * mm, v(-10.5, -13.4) * mm, v(-10.58, -5.11) * mm, v(-10.53, 4.85) * mm]});
            skFitSpline(sketch, "E295", {"points": [v(-2, 25.96) * mm, v(2.66, 27.62) * mm, v(6.65, 28.9) * mm, v(6.88, 28.8) * mm]});
            skFitSpline(sketch, "E296", {"points": [v(6.88, 28.8) * mm, v(7.2, 28.67) * mm, v(7.27, 23.97) * mm, v(7.2, 6.22) * mm]});
            skFitSpline(sketch, "E297", {"points": [v(7.2, 6.22) * mm, v(7.13, -13.39) * mm, v(7.06, -16.2) * mm, v(6.63, -16.26) * mm]});
            skFitSpline(sketch, "E298", {"points": [v(6.63, -16.26) * mm, v(6.36, -16.3) * mm, v(2.5, -15.77) * mm, v(-1.96, -15.1) * mm]});
            skLineSegment(sketch, "E299", {"start": v(41.44, 26.13) * mm, "end": v(41.44, -19.92) * mm});
            skLineSegment(sketch, "E300", {"start": v(41.44, -19.92) * mm, "end": v(42.33, -19.76) * mm});
            skFitSpline(sketch, "E301", {"points": [v(2.8, 26.6) * mm, v(0.88, 25.92) * mm, v(-2.67, 24.66) * mm, v(-5.08, 23.8) * mm]});
            skLineSegment(sketch, "E302", {"start": v(-10.53, 4.85) * mm, "end": v(-10.45, 22.96) * mm});
            skLineSegment(sketch, "E303", {"start": v(-10.45, 22.96) * mm, "end": v(-2, 25.96) * mm});
            skFitSpline(sketch, "E304", {"points": [v(-2.24, -14.1) * mm, v(1.83, -14.7) * mm, v(5.42, -15.22) * mm, v(5.74, -15.25) * mm]});
            skFitSpline(sketch, "E305", {"points": [v(5.74, -15.25) * mm, v(6.27, -15.3) * mm, v(6.3, -14.05) * mm, v(6.3, 6.26) * mm]});
            skLineSegment(sketch, "E306", {"start": v(6.3, 6.26) * mm, "end": v(6.3, 27.83) * mm});
            skLineSegment(sketch, "E307", {"start": v(6.3, 27.83) * mm, "end": v(2.8, 26.6) * mm});
            skFitSpline(sketch, "E308", {"points": [v(72.57, -16.16) * mm, v(72.44, -16.02) * mm, v(72.34, -5.8) * mm, v(72.34, 6.54) * mm]});
            skFitSpline(sketch, "E309", {"points": [v(72.34, 6.54) * mm, v(72.34, 24.26) * mm, v(72.43, 28.98) * mm, v(72.75, 28.96) * mm]});
            skFitSpline(sketch, "E310", {"points": [v(72.75, 28.96) * mm, v(72.97, 28.95) * mm, v(76.89, 27.6) * mm, v(81.45, 25.95) * mm]});
            skFitSpline(sketch, "E311", {"points": [v(88.7, -14) * mm, v(88.02, -14.1) * mm, v(84.54, -14.62) * mm, v(80.96, -15.12) * mm]});
            skFitSpline(sketch, "E312", {"points": [v(80.96, -15.12) * mm, v(77.38, -15.63) * mm, v(74.08, -16.13) * mm, v(73.63, -16.23) * mm]});
            skFitSpline(sketch, "E313", {"points": [v(73.63, -16.23) * mm, v(73.17, -16.33) * mm, v(72.7, -16.3) * mm, v(72.57, -16.16) * mm]});
            skLineSegment(sketch, "E314", {"start": v(-5.08, 23.8) * mm, "end": v(-9.47, 22.23) * mm});
            skLineSegment(sketch, "E315", {"start": v(-9.47, 22.23) * mm, "end": v(-9.56, 4.62) * mm});
            skLineSegment(sketch, "E316", {"start": v(-9.56, 4.62) * mm, "end": v(-9.64, -12.98) * mm});
            skLineSegment(sketch, "E317", {"start": v(-9.64, -12.98) * mm, "end": v(-2.24, -14.1) * mm});
            skFitSpline(sketch, "E318", {"points": [v(81.53, 24.84) * mm, v(77.28, 26.37) * mm, v(73.62, 27.7) * mm, v(73.4, 27.8) * mm]});
            skFitSpline(sketch, "E319", {"points": [v(73.4, 27.8) * mm, v(73.08, 27.93) * mm, v(73, 23.48) * mm, v(73, 6.3) * mm]});
            skLineSegment(sketch, "E320", {"start": v(81.45, 25.95) * mm, "end": v(89.75, 22.97) * mm});
            skLineSegment(sketch, "E321", {"start": v(89.75, 22.97) * mm, "end": v(89.83, 4.6) * mm});
            skLineSegment(sketch, "E322", {"start": v(89.83, 4.6) * mm, "end": v(89.91, -13.78) * mm});
            skLineSegment(sketch, "E323", {"start": v(89.91, -13.78) * mm, "end": v(88.7, -14) * mm});
            skFitSpline(sketch, "E324", {"points": [v(73.89, -15.2) * mm, v(74.38, -15.1) * mm, v(78.04, -14.55) * mm, v(82.02, -13.99) * mm]});
            skLineSegment(sketch, "E325", {"start": v(82.02, -13.99) * mm, "end": v(89.26, -12.96) * mm});
            skLineSegment(sketch, "E326", {"start": v(89.26, -12.96) * mm, "end": v(89.26, 4.55) * mm});
            skLineSegment(sketch, "E327", {"start": v(89.26, 4.55) * mm, "end": v(89.26, 22.06) * mm});
            skLineSegment(sketch, "E328", {"start": v(89.26, 22.06) * mm, "end": v(81.53, 24.84) * mm});
            skFitSpline(sketch, "E329", {"points": [v(-26.27, -11.53) * mm, v(-26.83, -11.4) * mm, v(-27.41, -11.3) * mm, v(-27.57, -11.3) * mm]});
            skFitSpline(sketch, "E330", {"points": [v(-27.57, -11.3) * mm, v(-27.72, -11.3) * mm, v(-27.85, -8.35) * mm, v(-27.85, -4.73) * mm]});
            skLineSegment(sketch, "E331", {"start": v(73, 6.3) * mm, "end": v(73, -15.39) * mm});
            skLineSegment(sketch, "E332", {"start": v(73, -15.39) * mm, "end": v(73.89, -15.2) * mm});
            skFitSpline(sketch, "E333", {"points": [v(-29.07, 1.63) * mm, v(-29.74, 1.5) * mm, v(-30.47, 1.4) * mm, v(-30.7, 1.4) * mm]});
            skFitSpline(sketch, "E334", {"points": [v(-30.7, 1.4) * mm, v(-31, 1.4) * mm, v(-31.1, -0.05) * mm, v(-31.1, -4.61) * mm]});
            skLineSegment(sketch, "E335", {"start": v(-14.84, -13.17) * mm, "end": v(-15.65, -12.9) * mm});
            skLineSegment(sketch, "E336", {"start": v(-15.65, -12.9) * mm, "end": v(-15.74, -5) * mm});
            skLineSegment(sketch, "E337", {"start": v(-15.74, -5) * mm, "end": v(-15.83, 2.89) * mm});
            skLineSegment(sketch, "E338", {"start": v(-15.83, 2.89) * mm, "end": v(-17.2, 2.78) * mm});
            skLineSegment(sketch, "E339", {"start": v(-17.2, 2.78) * mm, "end": v(-18.58, 2.67) * mm});
            skLineSegment(sketch, "E340", {"start": v(-18.58, 2.67) * mm, "end": v(-18.67, -4.88) * mm});
            skLineSegment(sketch, "E341", {"start": v(-18.67, -4.88) * mm, "end": v(-18.76, -12.43) * mm});
            skLineSegment(sketch, "E342", {"start": v(-18.76, -12.43) * mm, "end": v(-20.3, -12.32) * mm});
            skLineSegment(sketch, "E343", {"start": v(-20.3, -12.32) * mm, "end": v(-21.83, -12.21) * mm});
            skLineSegment(sketch, "E344", {"start": v(-21.83, -12.21) * mm, "end": v(-21.92, -5.03) * mm});
            skLineSegment(sketch, "E345", {"start": v(-21.92, -5.03) * mm, "end": v(-22.01, 2.16) * mm});
            skLineSegment(sketch, "E346", {"start": v(-22.01, 2.16) * mm, "end": v(-23.55, 2.05) * mm});
            skLineSegment(sketch, "E347", {"start": v(-23.55, 2.05) * mm, "end": v(-25.09, 1.94) * mm});
            skLineSegment(sketch, "E348", {"start": v(-25.09, 1.94) * mm, "end": v(-25.18, -4.9) * mm});
            skLineSegment(sketch, "E349", {"start": v(-25.18, -4.9) * mm, "end": v(-25.26, -11.76) * mm});
            skLineSegment(sketch, "E350", {"start": v(-25.26, -11.76) * mm, "end": v(-26.27, -11.53) * mm});
            skFitSpline(sketch, "E351", {"points": [v(-23.16, 35.43) * mm, v(-17.62, 38.89) * mm, v(-12.9, 41.63) * mm, v(-12.66, 41.53) * mm]});
            skFitSpline(sketch, "E352", {"points": [v(-12.66, 41.53) * mm, v(-12.31, 41.38) * mm, v(-12.25, 36.38) * mm, v(-12.32, 14.02) * mm]});
            skLineSegment(sketch, "E353", {"start": v(-27.85, -4.73) * mm, "end": v(-27.85, 1.86) * mm});
            skLineSegment(sketch, "E354", {"start": v(-27.85, 1.86) * mm, "end": v(-29.07, 1.63) * mm});
            skFitSpline(sketch, "E355", {"points": [v(-13.21, -13.37) * mm, v(-13.66, -13.4) * mm, v(-14.4, -13.31) * mm, v(-14.84, -13.17) * mm]});
            skLineSegment(sketch, "E356", {"start": v(-31.1, -4.61) * mm, "end": v(-31.1, -10.63) * mm});
            skLineSegment(sketch, "E357", {"start": v(-31.1, -10.63) * mm, "end": v(-32.16, -10.51) * mm});
            skLineSegment(sketch, "E358", {"start": v(-32.16, -10.51) * mm, "end": v(-33.22, -10.4) * mm});
            skLineSegment(sketch, "E359", {"start": v(-33.22, -10.4) * mm, "end": v(-33.22, 9.38) * mm});
            skLineSegment(sketch, "E360", {"start": v(-33.22, 9.38) * mm, "end": v(-33.22, 29.16) * mm});
            skLineSegment(sketch, "E361", {"start": v(-33.22, 29.16) * mm, "end": v(-23.16, 35.43) * mm});
            skFitSpline(sketch, "E362", {"points": [v(-13.21, 13.92) * mm, v(-13.21, 28.4) * mm, v(-13.28, 40.23) * mm, v(-13.37, 40.23) * mm]});
            skFitSpline(sketch, "E363", {"points": [v(-13.37, 40.23) * mm, v(-13.45, 40.23) * mm, v(-17.77, 37.59) * mm, v(-22.97, 34.35) * mm]});
            skFitSpline(sketch, "E364", {"points": [v(-32.4, 9.3) * mm, v(-32.4, -3.23) * mm, v(-32.3, -9.85) * mm, v(-32.08, -9.85) * mm]});
            skFitSpline(sketch, "E365", {"points": [v(-32.08, -9.85) * mm, v(-31.88, -9.85) * mm, v(-31.76, -7.56) * mm, v(-31.76, -3.68) * mm]});
            skLineSegment(sketch, "E366", {"start": v(-12.32, 14.02) * mm, "end": v(-12.4, -13.3) * mm});
            skLineSegment(sketch, "E367", {"start": v(-12.4, -13.3) * mm, "end": v(-13.21, -13.37) * mm});
            skFitSpline(sketch, "E368", {"points": [v(-30.21, 2.5) * mm, v(-29.36, 2.5) * mm, v(-28.34, 2.6) * mm, v(-27.93, 2.71) * mm]});
            skLineSegment(sketch, "E369", {"start": v(-22.97, 34.35) * mm, "end": v(-32.4, 28.47) * mm});
            skLineSegment(sketch, "E370", {"start": v(-32.4, 28.47) * mm, "end": v(-32.4, 9.3) * mm});
            skFitSpline(sketch, "E371", {"points": [v(-27.2, -3.82) * mm, v(-27.2, -10.34) * mm, v(-27.18, -10.58) * mm, v(-26.55, -10.58) * mm]});
            skFitSpline(sketch, "E372", {"points": [v(-26.55, -10.58) * mm, v(-25.92, -10.58) * mm, v(-25.9, -10.34) * mm, v(-25.9, -3.91) * mm]});
            skLineSegment(sketch, "E373", {"start": v(-31.76, -3.68) * mm, "end": v(-31.76, 2.49) * mm});
            skLineSegment(sketch, "E374", {"start": v(-31.76, 2.49) * mm, "end": v(-30.21, 2.5) * mm});
            skFitSpline(sketch, "E375", {"points": [v(-24.88, 2.98) * mm, v(-24.32, 3.1) * mm, v(-23.3, 3.21) * mm, v(-22.6, 3.21) * mm]});
            skLineSegment(sketch, "E376", {"start": v(-27.93, 2.71) * mm, "end": v(-27.2, 2.93) * mm});
            skLineSegment(sketch, "E377", {"start": v(-27.2, 2.93) * mm, "end": v(-27.2, -3.82) * mm});
            skFitSpline(sketch, "E378", {"points": [v(-19.72, -4.07) * mm, v(-19.72, -0.09) * mm, v(-19.6, 3.24) * mm, v(-19.48, 3.33) * mm]});
            skFitSpline(sketch, "E379", {"points": [v(-19.48, 3.33) * mm, v(-19.34, 3.43) * mm, v(-18.24, 3.62) * mm, v(-17.04, 3.76) * mm]});
            skLineSegment(sketch, "E380", {"start": v(-25.9, -3.91) * mm, "end": v(-25.9, 2.76) * mm});
            skLineSegment(sketch, "E381", {"start": v(-25.9, 2.76) * mm, "end": v(-24.88, 2.98) * mm});
            skFitSpline(sketch, "E382", {"points": [v(91.86, 14.06) * mm, v(91.86, 32.34) * mm, v(91.97, 41.69) * mm, v(92.19, 41.69) * mm]});
            skFitSpline(sketch, "E383", {"points": [v(92.19, 41.69) * mm, v(92.53, 41.69) * mm, v(111.55, 29.92) * mm, v(112.28, 29.26) * mm]});
            skFitSpline(sketch, "E384", {"points": [v(112.28, 29.26) * mm, v(112.6, 28.97) * mm, v(112.67, 24.68) * mm, v(112.6, 9.24) * mm]});
            skLineSegment(sketch, "E385", {"start": v(-22.6, 3.21) * mm, "end": v(-21.35, 3.21) * mm});
            skLineSegment(sketch, "E386", {"start": v(-21.35, 3.21) * mm, "end": v(-21.35, -4.05) * mm});
            skLineSegment(sketch, "E387", {"start": v(-21.35, -4.05) * mm, "end": v(-21.35, -11.3) * mm});
            skLineSegment(sketch, "E388", {"start": v(-21.35, -11.3) * mm, "end": v(-20.53, -11.3) * mm});
            skLineSegment(sketch, "E389", {"start": v(-20.53, -11.3) * mm, "end": v(-19.72, -11.3) * mm});
            skLineSegment(sketch, "E390", {"start": v(-19.72, -11.3) * mm, "end": v(-19.72, -4.07) * mm});
            skFitSpline(sketch, "E391", {"points": [v(109.5, 1.53) * mm, v(108.84, 1.65) * mm, v(108.1, 1.75) * mm, v(107.88, 1.76) * mm]});
            skFitSpline(sketch, "E392", {"points": [v(107.88, 1.76) * mm, v(107.57, 1.76) * mm, v(107.47, 0.22) * mm, v(107.47, -4.73) * mm]});
            skLineSegment(sketch, "E393", {"start": v(-17.04, 3.76) * mm, "end": v(-14.84, 4.02) * mm});
            skLineSegment(sketch, "E394", {"start": v(-14.84, 4.02) * mm, "end": v(-14.84, -4.19) * mm});
            skLineSegment(sketch, "E395", {"start": v(-14.84, -4.19) * mm, "end": v(-14.84, -12.4) * mm});
            skLineSegment(sketch, "E396", {"start": v(-14.84, -12.4) * mm, "end": v(-14.03, -12.4) * mm});
            skLineSegment(sketch, "E397", {"start": v(-14.03, -12.4) * mm, "end": v(-13.21, -12.4) * mm});
            skLineSegment(sketch, "E398", {"start": v(-13.21, -12.4) * mm, "end": v(-13.21, 13.92) * mm});
            skLineSegment(sketch, "E399", {"start": v(-13.21, 13.92) * mm, "end": v(-13.21, 13.92) * mm});
            skFitSpline(sketch, "E400", {"points": [v(106.46, -11.44) * mm, v(105.9, -11.57) * mm, v(105.32, -11.67) * mm, v(105.16, -11.67) * mm]});
            skFitSpline(sketch, "E401", {"points": [v(105.16, -11.67) * mm, v(105.01, -11.67) * mm, v(104.85, -8.6) * mm, v(104.8, -4.86) * mm]});
            skLineSegment(sketch, "E402", {"start": v(112.6, 9.24) * mm, "end": v(112.52, -10.4) * mm});
            skLineSegment(sketch, "E403", {"start": v(112.52, -10.4) * mm, "end": v(111.62, -10.51) * mm});
            skLineSegment(sketch, "E404", {"start": v(111.62, -10.51) * mm, "end": v(110.73, -10.63) * mm});
            skLineSegment(sketch, "E405", {"start": v(110.73, -10.63) * mm, "end": v(110.73, -4.66) * mm});
            skLineSegment(sketch, "E406", {"start": v(110.73, -4.66) * mm, "end": v(110.73, 1.3) * mm});
            skLineSegment(sketch, "E407", {"start": v(110.73, 1.3) * mm, "end": v(109.5, 1.53) * mm});
            skFitSpline(sketch, "E408", {"points": [v(101.62, -4.9) * mm, v(101.62, -12.69) * mm, v(101.7, -12.4) * mm, v(99.48, -12.4) * mm]});
            skLineSegment(sketch, "E409", {"start": v(107.47, -4.73) * mm, "end": v(107.47, -11.22) * mm});
            skLineSegment(sketch, "E410", {"start": v(107.47, -11.22) * mm, "end": v(106.46, -11.44) * mm});
            skFitSpline(sketch, "E411", {"points": [v(95.44, -4.91) * mm, v(95.44, -9.2) * mm, v(95.33, -12.8) * mm, v(95.2, -12.88) * mm]});
            skFitSpline(sketch, "E412", {"points": [v(95.2, -12.88) * mm, v(95.06, -12.98) * mm, v(94.25, -13.17) * mm, v(93.4, -13.3) * mm]});
            skLineSegment(sketch, "E413", {"start": v(104.8, -4.86) * mm, "end": v(104.7, 1.94) * mm});
            skLineSegment(sketch, "E414", {"start": v(104.7, 1.94) * mm, "end": v(103.16, 2.05) * mm});
            skLineSegment(sketch, "E415", {"start": v(103.16, 2.05) * mm, "end": v(101.62, 2.16) * mm});
            skLineSegment(sketch, "E416", {"start": v(101.62, 2.16) * mm, "end": v(101.62, -4.9) * mm});
            skLineSegment(sketch, "E417", {"start": v(99.48, -12.4) * mm, "end": v(98.38, -12.4) * mm});
            skLineSegment(sketch, "E418", {"start": v(98.38, -12.4) * mm, "end": v(98.3, -4.86) * mm});
            skLineSegment(sketch, "E419", {"start": v(98.3, -4.86) * mm, "end": v(98.2, 2.67) * mm});
            skLineSegment(sketch, "E420", {"start": v(98.2, 2.67) * mm, "end": v(96.82, 2.78) * mm});
            skLineSegment(sketch, "E421", {"start": v(96.82, 2.78) * mm, "end": v(95.44, 2.9) * mm});
            skLineSegment(sketch, "E422", {"start": v(95.44, 2.9) * mm, "end": v(95.44, -4.91) * mm});
            skFitSpline(sketch, "E423", {"points": [v(96.66, 3.76) * mm, v(97.87, 3.62) * mm, v(98.96, 3.43) * mm, v(99.1, 3.33) * mm]});
            skFitSpline(sketch, "E424", {"points": [v(99.1, 3.33) * mm, v(99.23, 3.24) * mm, v(99.34, -0.09) * mm, v(99.34, -4.07) * mm]});
            skLineSegment(sketch, "E425", {"start": v(93.4, -13.3) * mm, "end": v(91.86, -13.57) * mm});
            skLineSegment(sketch, "E426", {"start": v(91.86, -13.57) * mm, "end": v(91.86, 14.06) * mm});
            skFitSpline(sketch, "E427", {"points": [v(102.23, 3.21) * mm, v(102.92, 3.21) * mm, v(103.95, 3.1) * mm, v(104.5, 2.98) * mm]});
            skLineSegment(sketch, "E428", {"start": v(94.46, -4.19) * mm, "end": v(94.46, 4.02) * mm});
            skLineSegment(sketch, "E429", {"start": v(94.46, 4.02) * mm, "end": v(96.66, 3.76) * mm});
            skFitSpline(sketch, "E430", {"points": [v(105.52, -3.91) * mm, v(105.52, -10.34) * mm, v(105.55, -10.58) * mm, v(106.17, -10.58) * mm]});
            skFitSpline(sketch, "E431", {"points": [v(106.17, -10.58) * mm, v(106.8, -10.58) * mm, v(106.82, -10.34) * mm, v(106.82, -3.82) * mm]});
            skLineSegment(sketch, "E432", {"start": v(99.34, -4.07) * mm, "end": v(99.34, -11.3) * mm});
            skLineSegment(sketch, "E433", {"start": v(99.34, -11.3) * mm, "end": v(100.15, -11.3) * mm});
            skLineSegment(sketch, "E434", {"start": v(100.15, -11.3) * mm, "end": v(100.97, -11.3) * mm});
            skLineSegment(sketch, "E435", {"start": v(100.97, -11.3) * mm, "end": v(100.97, -4.05) * mm});
            skLineSegment(sketch, "E436", {"start": v(100.97, -4.05) * mm, "end": v(100.97, 3.21) * mm});
            skLineSegment(sketch, "E437", {"start": v(100.97, 3.21) * mm, "end": v(102.23, 3.21) * mm});
            skFitSpline(sketch, "E438", {"points": [v(107.56, 2.71) * mm, v(107.96, 2.6) * mm, v(108.98, 2.5) * mm, v(109.83, 2.5) * mm]});
            skLineSegment(sketch, "E439", {"start": v(104.5, 2.98) * mm, "end": v(105.52, 2.76) * mm});
            skLineSegment(sketch, "E440", {"start": v(105.52, 2.76) * mm, "end": v(105.52, -3.91) * mm});
            skFitSpline(sketch, "E441", {"points": [v(111.46, -3.77) * mm, v(111.51, -7.22) * mm, v(111.59, -1.36) * mm, v(111.63, 9.24) * mm]});
            skLineSegment(sketch, "E442", {"start": v(106.82, -3.82) * mm, "end": v(106.82, 2.93) * mm});
            skLineSegment(sketch, "E443", {"start": v(106.82, 2.93) * mm, "end": v(107.56, 2.71) * mm});
            skFitSpline(sketch, "E444", {"points": [v(102.3, 34.38) * mm, v(97.12, 37.6) * mm, v(92.8, 40.23) * mm, v(92.7, 40.23) * mm]});
            skFitSpline(sketch, "E445", {"points": [v(92.7, 40.23) * mm, v(92.6, 40.23) * mm, v(92.51, 28.4) * mm, v(92.51, 13.92) * mm]});
            skLineSegment(sketch, "E446", {"start": v(109.83, 2.5) * mm, "end": v(111.36, 2.49) * mm});
            skLineSegment(sketch, "E447", {"start": v(111.36, 2.49) * mm, "end": v(111.46, -3.77) * mm});
            skFitSpline(sketch, "E448", {"points": [v(-10.47, 25.82) * mm, v(-10.55, 26.07) * mm, v(-10.58, 29.79) * mm, v(-10.54, 34.07) * mm]});
            skLineSegment(sketch, "E449", {"start": v(111.63, 9.24) * mm, "end": v(111.7, 28.52) * mm});
            skLineSegment(sketch, "E450", {"start": v(111.7, 28.52) * mm, "end": v(102.3, 34.38) * mm});
            skFitSpline(sketch, "E451", {"points": [v(-9.47, 41.81) * mm, v(-8.94, 41.78) * mm, v(-6.34, 40.9) * mm, v(-3.7, 39.87) * mm]});
            skLineSegment(sketch, "E452", {"start": v(92.51, 13.92) * mm, "end": v(92.51, -12.4) * mm});
            skLineSegment(sketch, "E453", {"start": v(92.51, -12.4) * mm, "end": v(93.49, -12.4) * mm});
            skLineSegment(sketch, "E454", {"start": v(93.49, -12.4) * mm, "end": v(94.46, -12.4) * mm});
            skLineSegment(sketch, "E455", {"start": v(94.46, -12.4) * mm, "end": v(94.46, -4.19) * mm});
            skFitSpline(sketch, "E456", {"points": [v(-4.24, 27.24) * mm, v(-10.1, 25.17) * mm, v(-10.23, 25.14) * mm, v(-10.47, 25.82) * mm]});
            skLineSegment(sketch, "E457", {"start": v(-10.54, 34.07) * mm, "end": v(-10.45, 41.87) * mm});
            skLineSegment(sketch, "E458", {"start": v(-10.45, 41.87) * mm, "end": v(-9.47, 41.81) * mm});
            skFitSpline(sketch, "E459", {"points": [v(-4.18, 38.97) * mm, v(-6.73, 39.93) * mm, v(-9, 40.79) * mm, v(-9.23, 40.88) * mm]});
            skFitSpline(sketch, "E460", {"points": [v(-9.23, 40.88) * mm, v(-9.54, 41) * mm, v(-9.63, 39.42) * mm, v(-9.63, 33.74) * mm]});
            skFitSpline(sketch, "E461", {"points": [v(-9.63, 33.74) * mm, v(-9.63, 29.73) * mm, v(-9.53, 26.45) * mm, v(-9.4, 26.47) * mm]});
            skFitSpline(sketch, "E462", {"points": [v(-9.4, 26.47) * mm, v(-9.26, 26.48) * mm, v(-7.02, 27.26) * mm, v(-4.43, 28.2) * mm]});
            skLineSegment(sketch, "E463", {"start": v(-3.7, 39.87) * mm, "end": v(1.1, 37.98) * mm});
            skLineSegment(sketch, "E464", {"start": v(1.1, 37.98) * mm, "end": v(1.1, 33.55) * mm});
            skLineSegment(sketch, "E465", {"start": v(1.1, 33.55) * mm, "end": v(1.1, 29.13) * mm});
            skLineSegment(sketch, "E466", {"start": v(1.1, 29.13) * mm, "end": v(-4.24, 27.24) * mm});
            skFitSpline(sketch, "E467", {"points": [v(83.74, 27.2) * mm, v(80.98, 28.2) * mm, v(78.6, 29.11) * mm, v(78.46, 29.2) * mm]});
            skFitSpline(sketch, "E468", {"points": [v(78.46, 29.2) * mm, v(78, 29.52) * mm, v(78.14, 37.56) * mm, v(78.6, 37.95) * mm]});
            skFitSpline(sketch, "E469", {"points": [v(78.6, 37.95) * mm, v(79.16, 38.43) * mm, v(88.66, 42.05) * mm, v(89.35, 42.05) * mm]});
            skFitSpline(sketch, "E470", {"points": [v(89.35, 42.05) * mm, v(89.86, 42.05) * mm, v(89.9, 41.33) * mm, v(89.9, 33.7) * mm]});
            skFitSpline(sketch, "E471", {"points": [v(89.9, 33.7) * mm, v(89.9, 25.99) * mm, v(89.86, 25.35) * mm, v(89.34, 25.37) * mm]});
            skFitSpline(sketch, "E472", {"points": [v(89.34, 25.37) * mm, v(89.03, 25.37) * mm, v(86.5, 26.2) * mm, v(83.74, 27.2) * mm]});
            skFitSpline(sketch, "E473", {"points": [v(89.26, 33.7) * mm, v(89.26, 37.7) * mm, v(89.15, 40.96) * mm, v(89.01, 40.96) * mm]});
            skFitSpline(sketch, "E474", {"points": [v(89.01, 40.96) * mm, v(88.88, 40.96) * mm, v(86.61, 40.12) * mm, v(83.97, 39.1) * mm]});
            skFitSpline(sketch, "E475", {"points": [v(83.81, 28.2) * mm, v(86.36, 27.28) * mm, v(88.63, 26.5) * mm, v(88.85, 26.48) * mm]});
            skFitSpline(sketch, "E476", {"points": [v(88.85, 26.48) * mm, v(89.17, 26.45) * mm, v(89.26, 28.11) * mm, v(89.26, 33.7) * mm]});
            skLineSegment(sketch, "E477", {"start": v(-4.43, 28.2) * mm, "end": v(0.29, 29.9) * mm});
            skLineSegment(sketch, "E478", {"start": v(0.29, 29.9) * mm, "end": v(0.38, 33.56) * mm});
            skLineSegment(sketch, "E479", {"start": v(0.38, 33.56) * mm, "end": v(0.47, 37.22) * mm});
            skLineSegment(sketch, "E480", {"start": v(0.47, 37.22) * mm, "end": v(-4.18, 38.97) * mm});
            skLineSegment(sketch, "E481", {"start": v(83.97, 39.1) * mm, "end": v(79.17, 37.23) * mm});
            skLineSegment(sketch, "E482", {"start": v(79.17, 37.23) * mm, "end": v(79.18, 33.56) * mm});
            skLineSegment(sketch, "E483", {"start": v(79.18, 33.56) * mm, "end": v(79.18, 29.89) * mm});
            skLineSegment(sketch, "E484", {"start": v(79.18, 29.89) * mm, "end": v(83.81, 28.2) * mm});
            skLineSegment(sketch, "E485", {"start": v(89.26, 33.7) * mm, "end": v(89.26, 33.7) * mm});
            skSolve(sketch);
        }
        {
            var Q0;
            Q0=makeQuery(id+"F0.imprint","IMPRINT",FACE,{"disambiguationData":[TD([[makeQuery(id+"F0.imprint","IMPRINT",EDGE,{"derivedFrom":sQuery(id+"F0.wireOp",EDGE,"E62")}),-1.0]])]});
            var Q1;
            Q1=makeQuery(id+"F0.imprint","IMPRINT",FACE,{"disambiguationData":[TD([[makeQuery(id+"F0.imprint","IMPRINT",EDGE,{"derivedFrom":sQuery(id+"F0.wireOp",EDGE,"E308")}),-1.0]])]});
            var Q2;
            Q2=makeQuery(id+"F0.imprint","IMPRINT",FACE,{"disambiguationData":[TD([[makeQuery(id+"F0.imprint","IMPRINT",EDGE,{"derivedFrom":sQuery(id+"F0.wireOp",EDGE,"E448")}),-1.0]])]});
            var Q3;
            Q3=makeQuery(id+"F0.imprint","IMPRINT",FACE,{"disambiguationData":[TD([[makeQuery(id+"F0.imprint","IMPRINT",EDGE,{"derivedFrom":sQuery(id+"F0.wireOp",EDGE,"E1")}),-1.0]])]});
            var Q4;
            Q4=makeQuery(id+"F0.imprint","IMPRINT",FACE,{"disambiguationData":[TD([[makeQuery(id+"F0.imprint","IMPRINT",EDGE,{"derivedFrom":sQuery(id+"F0.wireOp",EDGE,"E329")}),-1.0]])]});
            var Q5;
            Q5=makeQuery(id+"F0.imprint","IMPRINT",FACE,{"disambiguationData":[TD([[makeQuery(id+"F0.imprint","IMPRINT",EDGE,{"derivedFrom":sQuery(id+"F0.wireOp",EDGE,"E293")}),-1.0]])]});
            var Q6;
            Q6=makeQuery(id+"F0.imprint","IMPRINT",FACE,{"disambiguationData":[TD([[makeQuery(id+"F0.imprint","IMPRINT",EDGE,{"derivedFrom":sQuery(id+"F0.wireOp",EDGE,"E467")}),-1.0]])]});
            var Q7;
            Q7=makeQuery(id+"F0.imprint","IMPRINT",FACE,{"disambiguationData":[TD([[makeQuery(id+"F0.imprint","IMPRINT",EDGE,{"derivedFrom":sQuery(id+"F0.wireOp",EDGE,"E382")}),-1.0]])]});
            extrude(context, id + "F1", {"entities" : qUnion([Q0, Q1, Q2, Q3, Q4, Q5, Q6, Q7]), "depth" : 25 * mm, "offsetDistance" : 25 * mm});
        }
    });
